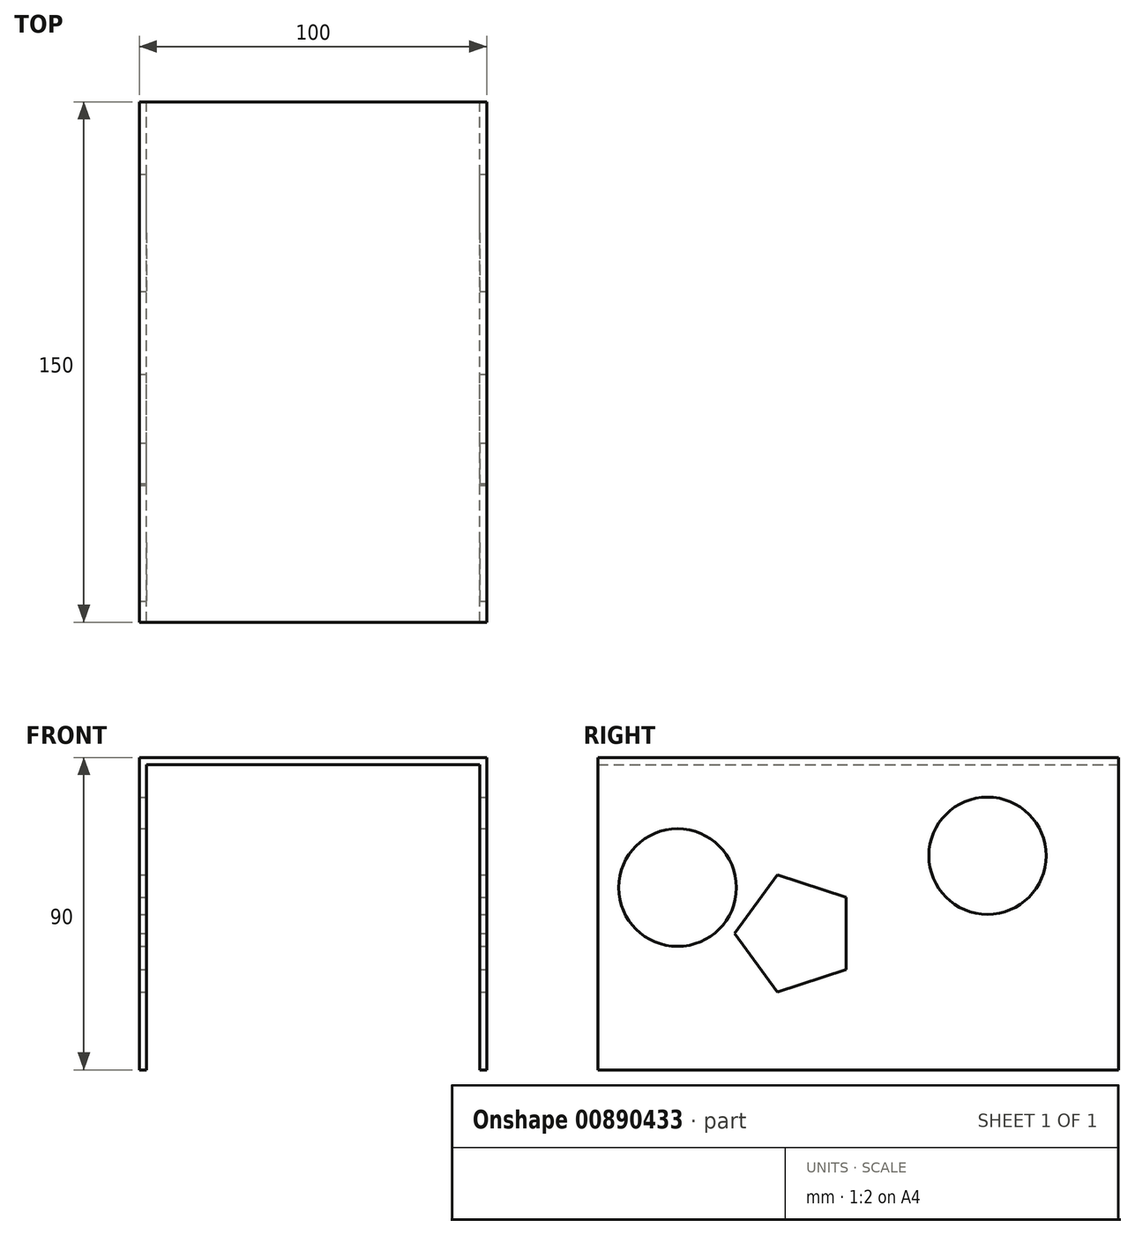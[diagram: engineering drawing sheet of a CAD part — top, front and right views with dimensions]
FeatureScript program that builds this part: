
annotation { "Feature Type Name" : "Feature", "Feature Type Description" : "" }
export const myFeature = defineFeature(function(context is Context, id is Id, definition is map)
    precondition{}
    {
        {
            var Q0;
            Q0=qCreatedBy(makeId("Front.planeOp"),FACE);
            var sketch = newSketch(context, id + "F0", { "sketchPlane" : qUnion([Q0])});
            skLineSegment(sketch, "E0.bottom", {"start": v(0, 0) * mm, "end": v(2, 0) * mm});
            skLineSegment(sketch, "E0.top", {"start": v(0, 90) * mm, "end": v(100, 90) * mm});
            skLineSegment(sketch, "E0.left", {"start": v(0, 0) * mm, "end": v(0, 90) * mm});
            skLineSegment(sketch, "E0.right", {"start": v(100, 0) * mm, "end": v(100, 90) * mm});
            skLineSegment(sketch, "E1.top", {"start": v(98, 88) * mm, "end": v(2, 88) * mm});
            skLineSegment(sketch, "E1.left", {"start": v(98, 0) * mm, "end": v(98, 88) * mm});
            skLineSegment(sketch, "E1.right", {"start": v(2, 0) * mm, "end": v(2, 88) * mm});
            skLineSegment(sketch, "E2.trimOffspring", {"start": v(98, 0) * mm, "end": v(100, 0) * mm});
            skSolve(sketch);
        }
        {
            var Q0;
            Q0 = qSketchRegion(id + "F0", true);
            extrude(context, id + "F1", {"entities" : qUnion([Q0]), "depth" : 150 * mm, "offsetDistance" : 25 * mm});
        }
        {
            var Q0;
            Q0=makeQuery(id+"F1.opExtrude","SWEPT_FACE",FACE,{"disambiguationData":[OSD([sQuery(id+"F0.wireOp",EDGE,"E0.right")])]});
            var sketch = newSketch(context, id + "F2", { "sketchPlane" : qUnion([Q0])});
            skCircle(sketch, "E3", {"center": v(-127, 52.53) * mm, "radius": 16.95 * mm});
            skCircle(sketch, "E4", {"center": v(-37.7, 61.72) * mm, "radius": 16.89 * mm});
            skCircle(sketch, "E5.cCircle", {"center": v(-92.82, 39.3) * mm, "radius": 14.33 * mm, "construction": true});
            skLineSegment(sketch, "E5.0", {"start": v(-78.5, 49.72) * mm, "end": v(-78.5, 28.9) * mm});
            skLineSegment(sketch, "E5.1", {"start": v(-78.5, 28.9) * mm, "end": v(-98.3, 22.46) * mm});
            skLineSegment(sketch, "E5.2", {"start": v(-98.3, 22.46) * mm, "end": v(-110.53, 39.3) * mm});
            skLineSegment(sketch, "E5.3", {"start": v(-110.53, 39.3) * mm, "end": v(-98.3, 56.15) * mm});
            skLineSegment(sketch, "E5.4", {"start": v(-98.3, 56.15) * mm, "end": v(-78.5, 49.72) * mm});
            skPoint(sketch, "E5.0.midPoint", {"position": v(-78.5, 39.3) * mm});
            skSolve(sketch);
        }
        {
            var Q0;
            Q0 = qSketchRegion(id + "F2", true);
            extrude(context, id + "F3", {"entities" : qUnion([Q0]), "operationType" : NewBodyOperationType.REMOVE, "oppositeDirection" : true, "depth" : 100 * mm, "offsetDistance" : 25 * mm});
        }
    });
